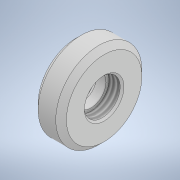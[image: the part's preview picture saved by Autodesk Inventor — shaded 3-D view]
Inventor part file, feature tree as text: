
AUTODESK INVENTOR PART (.ipt)
format: ipt  version: 2022 (Build 260153000, 153)  size: 163,328 bytes
history: native  units: mm
features: sketch x3, revolve x2, other x1, hole x1, thread x1
ambient origin geometry x8: Origin, YZ Plane, XZ Plane, XY Plane, X Axis, Y Axis, Z Axis, Center Point
bodies: Body1 (feature_tree)
feature tree (8):
  other  "Твердое тело1"
  revolve  "Вращение1"
  hole  "Отверстие1"  [1 undecoded]
  revolve  "Вращение2"
  thread  "Резьба1"
  sketch  "Эскиз1"
  sketch  "Эскиз2"
  sketch  "Эскиз3"
note: 1 required parameter value undecoded (feature->parameter linkage not recoverable at this tier; creation-order binding heuristic only, values carry confidence <= 0.55)
